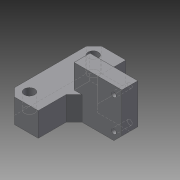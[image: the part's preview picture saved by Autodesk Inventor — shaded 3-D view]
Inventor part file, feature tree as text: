
AUTODESK INVENTOR PART (.ipt)
format: ipt  version: 2015 (Build 190159000, 159)  size: 127,488 bytes
history: native  units: mm
features: sketch x4, extrude x3, chamfer x3, hole x1
ambient origin geometry x8: Origin, YZ Plane, XZ Plane, XY Plane, X Axis, Y Axis, Z Axis, Center Point
bodies: Solid1 (feature_tree)
feature tree (11):
  extrude  "Extrusion1"  Depth=20.0mm
  extrude  "Extrusion2"  Depth=15.0mm
  extrude  "Extrusion3"  Depth=7.0mm
  hole  "Hole1"  [1 undecoded]
  chamfer  "Chamfer1"  Distance=6.5mm
  chamfer  "Chamfer2"  Distance=10.0mm
  chamfer  "Chamfer3"  Distance=10.0mm
  sketch  "Sketch1"  dims[d0=55.0mm d1=20.0mm]
  sketch  "Sketch2"  dims[d2=15.0mm d3=0.0mm d4=40.0mm]
  sketch  "Sketch3"  dims[d5=7.5mm d6=7.0mm]
  sketch  "Sketch4"  dims[d7=7.5mm d8=6.5mm d9=6.5mm d10=10.0mm d11=0.0mm d12=10.0mm d13=5.0mm d14=30.0mm d15=30.0mm d16=0.0mm d17=5.0mm d18=5.0mm d19=5.0mm d20=5.0mm d21=3.0mm d22=6.0mm d23=6.0mm d24=2.0mm d25=90.0deg d26=10.0mm d27=20.594885mm d28=5.0mm d29=2.0mm d30=45.0deg d31=5.0mm d32=2.0mm d33=45.0deg d34=5.0mm d35=2.0mm d36=45.0deg]
note: 1 required parameter value undecoded (feature->parameter linkage not recoverable at this tier; creation-order binding heuristic only, values carry confidence <= 0.55)
